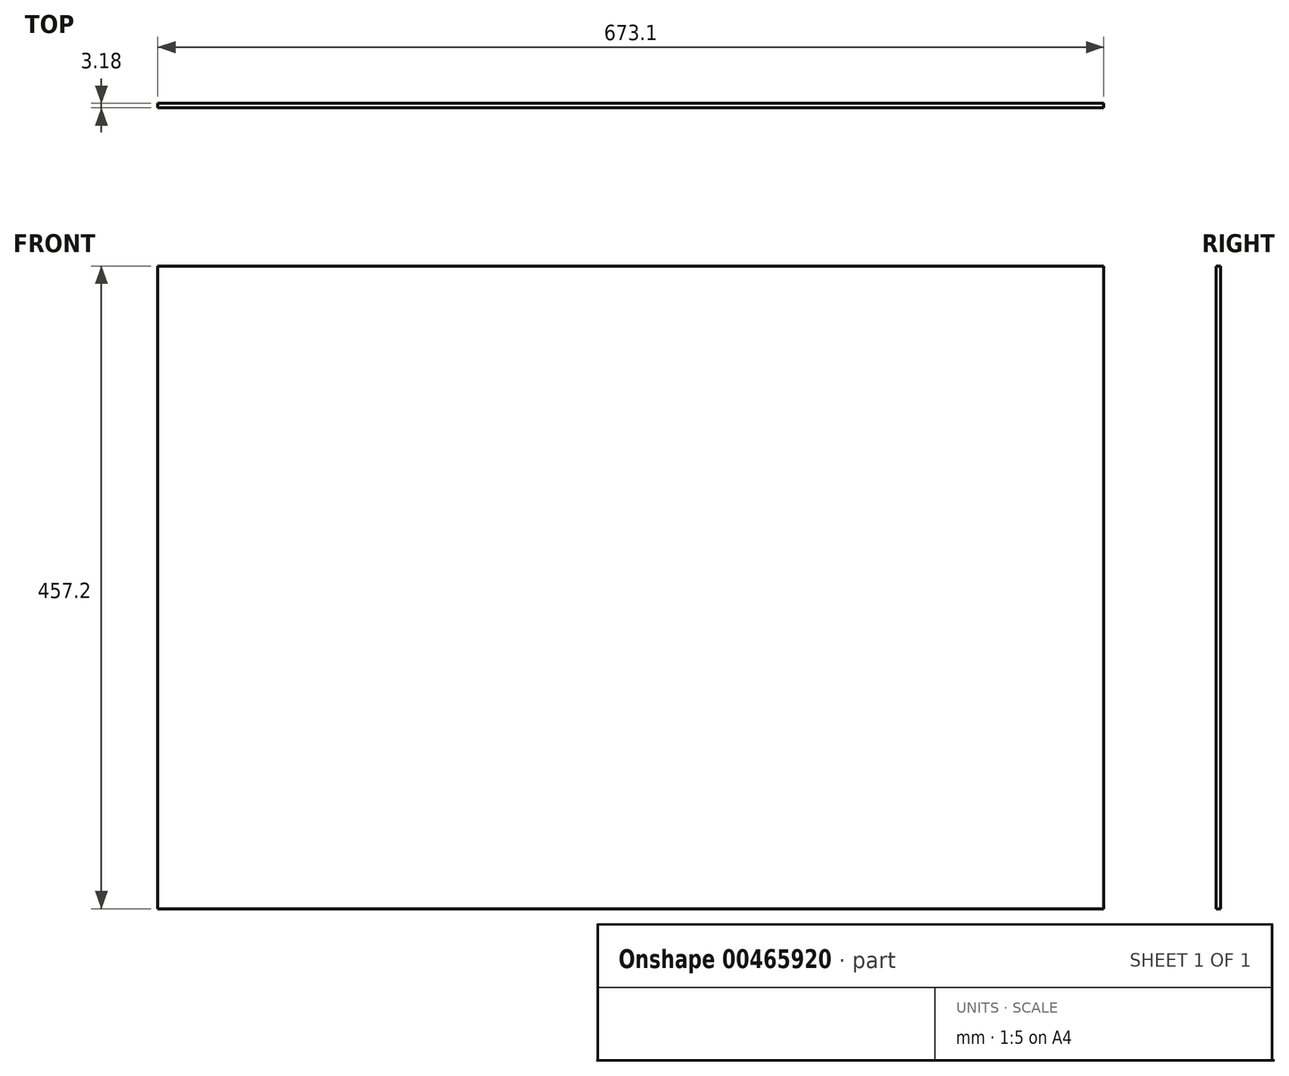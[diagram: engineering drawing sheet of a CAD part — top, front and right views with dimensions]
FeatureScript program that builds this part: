
annotation { "Feature Type Name" : "Feature", "Feature Type Description" : "" }
export const myFeature = defineFeature(function(context is Context, id is Id, definition is map)
    precondition{}
    {
        {
            var Q0;
            Q0=qCreatedBy(makeId("Front.planeOp"),FACE);
            var sketch = newSketch(context, id + "F0", { "sketchPlane" : qUnion([Q0])});
            skLineSegment(sketch, "E0.bottom", {"start": v(-336.55, 228.6) * mm, "end": v(336.55, 228.6) * mm});
            skLineSegment(sketch, "E0.top", {"start": v(-336.55, -228.6) * mm, "end": v(336.55, -228.6) * mm});
            skLineSegment(sketch, "E0.left", {"start": v(-336.55, 228.6) * mm, "end": v(-336.55, -228.6) * mm});
            skLineSegment(sketch, "E0.right", {"start": v(336.55, 228.6) * mm, "end": v(336.55, -228.6) * mm});
            skPoint(sketch, "E0.middle", {"position": v(0, 0) * mm});
            skSolve(sketch);
        }
        {
            var Q0;
            Q0=makeQuery(id+"F0.imprint","IMPRINT",FACE,{"disambiguationData":[TD([[makeQuery(id+"F0.imprint","IMPRINT",EDGE,{"derivedFrom":sQuery(id+"F0.wireOp",EDGE,"E0.bottom")}),-1.0]])]});
            extrude(context, id + "F1", {"entities" : qUnion([Q0]), "endBound" : BoundingType.SYMMETRIC, "depth" : 3.17 * mm});
        }
    });
